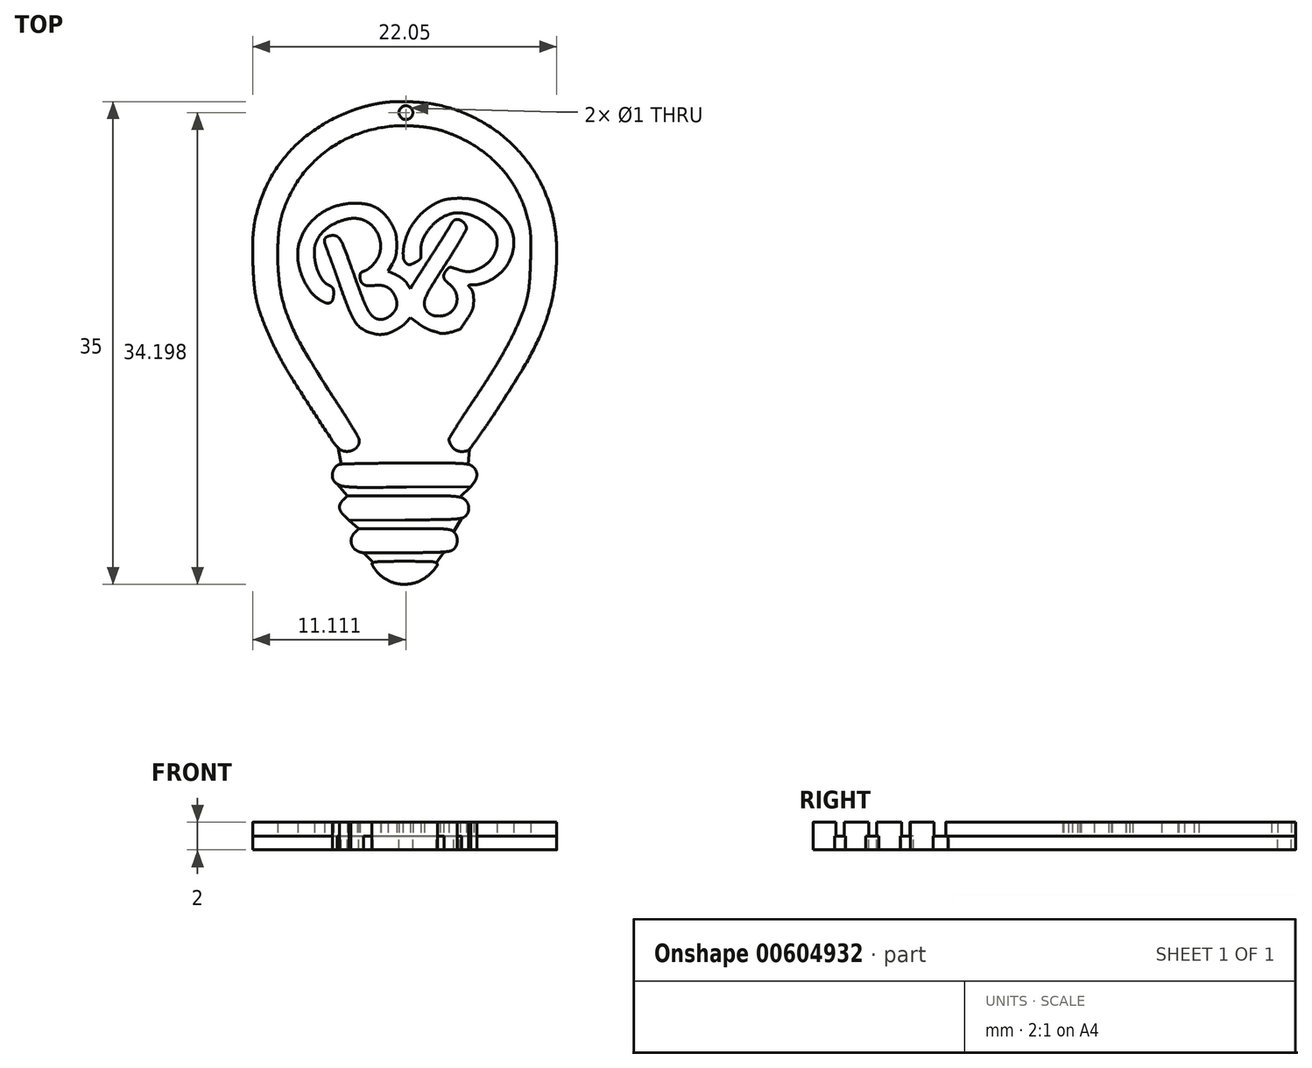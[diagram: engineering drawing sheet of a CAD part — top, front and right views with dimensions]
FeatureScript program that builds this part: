
annotation { "Feature Type Name" : "Feature", "Feature Type Description" : "" }
export const myFeature = defineFeature(function(context is Context, id is Id, definition is map)
    precondition{}
    {
        {
            var Q0;
            Q0=qCreatedBy(makeId("Top.planeOp"),FACE);
            var sketch = newSketch(context, id + "F0", { "sketchPlane" : qUnion([Q0])});
            skArc(sketch, "E0", {"start": v(-18.77, 20.13) * mm, "mid": v(-19.22, 20.06) * mm, "end": v(-19.67, 19.97) * mm});
            skArc(sketch, "E1", {"start": v(-19.67, 19.97) * mm, "mid": v(-20.1, 19.88) * mm, "end": v(-20.5, 19.76) * mm});
            skArc(sketch, "E2", {"start": v(-20.5, 19.76) * mm, "mid": v(-20.92, 19.63) * mm, "end": v(-21.33, 19.48) * mm});
            skArc(sketch, "E3", {"start": v(-21.33, 19.48) * mm, "mid": v(-21.77, 19.3) * mm, "end": v(-22.2, 19.1) * mm});
            skArc(sketch, "E4", {"start": v(-22.2, 19.1) * mm, "mid": v(-23.39, 18.47) * mm, "end": v(-24.49, 17.7) * mm});
            skArc(sketch, "E5", {"start": v(-24.49, 17.7) * mm, "mid": v(-25.46, 16.82) * mm, "end": v(-26.31, 15.83) * mm});
            skArc(sketch, "E6", {"start": v(-26.31, 15.83) * mm, "mid": v(-27.03, 14.75) * mm, "end": v(-27.6, 13.6) * mm});
            skArc(sketch, "E7", {"start": v(-27.6, 13.6) * mm, "mid": v(-28.02, 12.36) * mm, "end": v(-28.3, 11.08) * mm});
            skArc(sketch, "E8", {"start": v(-28.3, 11.08) * mm, "mid": v(-28.35, 10.53) * mm, "end": v(-28.38, 10) * mm});
            skArc(sketch, "E9", {"start": v(-28.38, 10) * mm, "mid": v(-28.38, 9.22) * mm, "end": v(-28.36, 8.44) * mm});
            skArc(sketch, "E10", {"start": v(-28.36, 8.44) * mm, "mid": v(-28.33, 7.67) * mm, "end": v(-28.27, 6.9) * mm});
            skArc(sketch, "E11", {"start": v(-28.27, 6.9) * mm, "mid": v(-28.21, 6.37) * mm, "end": v(-28.11, 5.84) * mm});
            skArc(sketch, "E12", {"start": v(-28.11, 5.84) * mm, "mid": v(-28, 5.38) * mm, "end": v(-27.86, 4.93) * mm});
            skArc(sketch, "E13", {"start": v(-27.86, 4.93) * mm, "mid": v(-27.67, 4.39) * mm, "end": v(-27.46, 3.85) * mm});
            skArc(sketch, "E14", {"start": v(-27.46, 3.85) * mm, "mid": v(-27.2, 3.27) * mm, "end": v(-26.94, 2.7) * mm});
            skArc(sketch, "E15", {"start": v(-26.94, 2.7) * mm, "mid": v(-26.66, 2.1) * mm, "end": v(-26.36, 1.53) * mm});
            skArc(sketch, "E16", {"start": v(-26.36, 1.53) * mm, "mid": v(-25.98, 0.88) * mm, "end": v(-25.6, 0.23) * mm});
            skArc(sketch, "E17", {"start": v(-25.6, 0.23) * mm, "mid": v(-24.89, -0.88) * mm, "end": v(-24.18, -2) * mm});
            skArc(sketch, "E18", {"start": v(-24.18, -2) * mm, "mid": v(-23.44, -3.12) * mm, "end": v(-22.7, -4.25) * mm});
            skArc(sketch, "E19", {"start": v(-22.7, -4.25) * mm, "mid": v(-22.46, -4.6) * mm, "end": v(-22.19, -4.91) * mm});
            skArc(sketch, "E20", {"start": v(-22.19, -4.91) * mm, "mid": v(-22, -5.07) * mm, "end": v(-21.76, -5.15) * mm});
            skArc(sketch, "E21", {"start": v(-21.76, -5.15) * mm, "mid": v(-21.5, -5.17) * mm, "end": v(-21.23, -5.13) * mm});
            skArc(sketch, "E22", {"start": v(-21.23, -5.13) * mm, "mid": v(-21, -5.02) * mm, "end": v(-20.8, -4.85) * mm});
            skArc(sketch, "E23", {"start": v(-20.8, -4.85) * mm, "mid": v(-20.69, -4.65) * mm, "end": v(-20.65, -4.43) * mm});
            skArc(sketch, "E24", {"start": v(-20.65, -4.43) * mm, "mid": v(-20.66, -4.3) * mm, "end": v(-20.7, -4.19) * mm});
            skArc(sketch, "E25", {"start": v(-20.7, -4.19) * mm, "mid": v(-20.88, -3.87) * mm, "end": v(-21.06, -3.55) * mm});
            skArc(sketch, "E26", {"start": v(-21.06, -3.55) * mm, "mid": v(-21.32, -3.13) * mm, "end": v(-21.58, -2.71) * mm});
            skArc(sketch, "E27", {"start": v(-21.58, -2.71) * mm, "mid": v(-21.94, -2.15) * mm, "end": v(-22.31, -1.58) * mm});
            skArc(sketch, "E28", {"start": v(-22.31, -1.58) * mm, "mid": v(-23.5, 0.26) * mm, "end": v(-24.63, 2.12) * mm});
            skArc(sketch, "E29", {"start": v(-24.63, 2.12) * mm, "mid": v(-25.3, 3.36) * mm, "end": v(-25.85, 4.64) * mm});
            skArc(sketch, "E30", {"start": v(-25.85, 4.64) * mm, "mid": v(-26.2, 5.76) * mm, "end": v(-26.42, 6.9) * mm});
            skArc(sketch, "E31", {"start": v(-26.42, 6.9) * mm, "mid": v(-26.54, 8.22) * mm, "end": v(-26.56, 9.55) * mm});
            skArc(sketch, "E32", {"start": v(-26.56, 9.55) * mm, "mid": v(-26.54, 10.12) * mm, "end": v(-26.5, 10.7) * mm});
            skArc(sketch, "E33", {"start": v(-26.5, 10.7) * mm, "mid": v(-26.44, 11.14) * mm, "end": v(-26.36, 11.58) * mm});
            skArc(sketch, "E34", {"start": v(-26.36, 11.58) * mm, "mid": v(-26.25, 12) * mm, "end": v(-26.11, 12.4) * mm});
            skArc(sketch, "E35", {"start": v(-26.11, 12.4) * mm, "mid": v(-25.93, 12.87) * mm, "end": v(-25.73, 13.33) * mm});
            skArc(sketch, "E36", {"start": v(-25.73, 13.33) * mm, "mid": v(-25.07, 14.49) * mm, "end": v(-24.24, 15.53) * mm});
            skArc(sketch, "E37", {"start": v(-24.24, 15.53) * mm, "mid": v(-23.26, 16.44) * mm, "end": v(-22.15, 17.2) * mm});
            skArc(sketch, "E38", {"start": v(-22.15, 17.2) * mm, "mid": v(-20.92, 17.78) * mm, "end": v(-19.62, 18.19) * mm});
            skArc(sketch, "E39", {"start": v(-19.62, 18.19) * mm, "mid": v(-18.26, 18.4) * mm, "end": v(-16.87, 18.43) * mm});
            skArc(sketch, "E40", {"start": v(-16.87, 18.43) * mm, "mid": v(-16.36, 18.39) * mm, "end": v(-15.84, 18.33) * mm});
            skArc(sketch, "E41", {"start": v(-15.84, 18.33) * mm, "mid": v(-15.4, 18.27) * mm, "end": v(-14.98, 18.17) * mm});
            skArc(sketch, "E42", {"start": v(-14.98, 18.17) * mm, "mid": v(-14.56, 18.05) * mm, "end": v(-14.16, 17.9) * mm});
            skArc(sketch, "E43", {"start": v(-14.16, 17.9) * mm, "mid": v(-13.7, 17.72) * mm, "end": v(-13.23, 17.51) * mm});
            skArc(sketch, "E44", {"start": v(-13.23, 17.51) * mm, "mid": v(-12.37, 17.04) * mm, "end": v(-11.55, 16.47) * mm});
            skArc(sketch, "E45", {"start": v(-11.55, 16.47) * mm, "mid": v(-10.82, 15.84) * mm, "end": v(-10.16, 15.12) * mm});
            skArc(sketch, "E46", {"start": v(-10.16, 15.12) * mm, "mid": v(-9.58, 14.34) * mm, "end": v(-9.1, 13.5) * mm});
            skArc(sketch, "E47", {"start": v(-9.1, 13.5) * mm, "mid": v(-8.71, 12.61) * mm, "end": v(-8.42, 11.68) * mm});
            skArc(sketch, "E48", {"start": v(-8.42, 11.68) * mm, "mid": v(-8.35, 11.38) * mm, "end": v(-8.3, 11.07) * mm});
            skArc(sketch, "E49", {"start": v(-8.3, 11.07) * mm, "mid": v(-8.25, 10.8) * mm, "end": v(-8.23, 10.52) * mm});
            skArc(sketch, "E50", {"start": v(-8.23, 10.52) * mm, "mid": v(-8.21, 10.17) * mm, "end": v(-8.2, 9.82) * mm});
            skArc(sketch, "E51", {"start": v(-8.2, 9.82) * mm, "mid": v(-8.22, 9.22) * mm, "end": v(-8.23, 8.62) * mm});
            skArc(sketch, "E52", {"start": v(-8.23, 8.62) * mm, "mid": v(-8.26, 7.83) * mm, "end": v(-8.31, 7.03) * mm});
            skArc(sketch, "E53", {"start": v(-8.31, 7.03) * mm, "mid": v(-8.37, 6.49) * mm, "end": v(-8.47, 5.95) * mm});
            skArc(sketch, "E54", {"start": v(-8.47, 5.95) * mm, "mid": v(-8.6, 5.44) * mm, "end": v(-8.78, 4.95) * mm});
            skArc(sketch, "E55", {"start": v(-8.78, 4.95) * mm, "mid": v(-9.04, 4.3) * mm, "end": v(-9.32, 3.68) * mm});
            skArc(sketch, "E56", {"start": v(-9.32, 3.68) * mm, "mid": v(-9.6, 3.08) * mm, "end": v(-9.91, 2.5) * mm});
            skArc(sketch, "E57", {"start": v(-9.91, 2.5) * mm, "mid": v(-10.26, 1.87) * mm, "end": v(-10.62, 1.25) * mm});
            skArc(sketch, "E58", {"start": v(-10.62, 1.25) * mm, "mid": v(-11.06, 0.53) * mm, "end": v(-11.51, -0.18) * mm});
            skArc(sketch, "E59", {"start": v(-11.51, -0.18) * mm, "mid": v(-12.09, -1.06) * mm, "end": v(-12.68, -1.94) * mm});
            skArc(sketch, "E60", {"start": v(-12.68, -1.94) * mm, "mid": v(-12.96, -2.36) * mm, "end": v(-13.24, -2.79) * mm});
            skArc(sketch, "E61", {"start": v(-13.24, -2.79) * mm, "mid": v(-13.48, -3.16) * mm, "end": v(-13.71, -3.54) * mm});
            skArc(sketch, "E62", {"start": v(-13.71, -3.54) * mm, "mid": v(-13.9, -3.86) * mm, "end": v(-14.1, -4.18) * mm});
            skArc(sketch, "E63", {"start": v(-14.1, -4.18) * mm, "mid": v(-14.13, -4.25) * mm, "end": v(-14.14, -4.33) * mm});
            skArc(sketch, "E64", {"start": v(-14.14, -4.33) * mm, "mid": v(-14.14, -4.38) * mm, "end": v(-14.12, -4.44) * mm});
            skArc(sketch, "E65", {"start": v(-14.12, -4.44) * mm, "mid": v(-14.1, -4.5) * mm, "end": v(-14.07, -4.58) * mm});
            skArc(sketch, "E66", {"start": v(-14.07, -4.58) * mm, "mid": v(-14.03, -4.66) * mm, "end": v(-13.99, -4.73) * mm});
            skArc(sketch, "E67", {"start": v(-13.99, -4.73) * mm, "mid": v(-13.94, -4.8) * mm, "end": v(-13.9, -4.87) * mm});
            skArc(sketch, "E68", {"start": v(-13.9, -4.87) * mm, "mid": v(-13.8, -4.97) * mm, "end": v(-13.68, -5.06) * mm});
            skArc(sketch, "E69", {"start": v(-13.68, -5.06) * mm, "mid": v(-13.55, -5.12) * mm, "end": v(-13.4, -5.16) * mm});
            skArc(sketch, "E70", {"start": v(-13.4, -5.16) * mm, "mid": v(-13.25, -5.18) * mm, "end": v(-13.1, -5.18) * mm});
            skArc(sketch, "E71", {"start": v(-13.1, -5.18) * mm, "mid": v(-12.93, -5.15) * mm, "end": v(-12.77, -5.1) * mm});
            skArc(sketch, "E72", {"start": v(-12.77, -5.1) * mm, "mid": v(-12.7, -5.07) * mm, "end": v(-12.66, -5.01) * mm});
            skArc(sketch, "E73", {"start": v(-12.66, -5.01) * mm, "mid": v(-12.42, -4.7) * mm, "end": v(-12.2, -4.38) * mm});
            skArc(sketch, "E74", {"start": v(-12.2, -4.38) * mm, "mid": v(-11.92, -4) * mm, "end": v(-11.66, -3.63) * mm});
            skArc(sketch, "E75", {"start": v(-11.66, -3.63) * mm, "mid": v(-11.36, -3.2) * mm, "end": v(-11.06, -2.76) * mm});
            skArc(sketch, "E76", {"start": v(-11.06, -2.76) * mm, "mid": v(-9.94, -1.04) * mm, "end": v(-8.86, 0.7) * mm});
            skArc(sketch, "E77", {"start": v(-8.86, 0.7) * mm, "mid": v(-8.17, 1.92) * mm, "end": v(-7.55, 3.19) * mm});
            skArc(sketch, "E78", {"start": v(-7.55, 3.19) * mm, "mid": v(-7.13, 4.24) * mm, "end": v(-6.8, 5.33) * mm});
            skArc(sketch, "E79", {"start": v(-6.8, 5.33) * mm, "mid": v(-6.55, 6.45) * mm, "end": v(-6.4, 7.58) * mm});
            skArc(sketch, "E80", {"start": v(-6.4, 7.58) * mm, "mid": v(-6.35, 8.52) * mm, "end": v(-6.33, 9.46) * mm});
            skArc(sketch, "E81", {"start": v(-6.33, 9.46) * mm, "mid": v(-6.37, 10.3) * mm, "end": v(-6.47, 11.12) * mm});
            skArc(sketch, "E82", {"start": v(-6.47, 11.12) * mm, "mid": v(-6.62, 11.9) * mm, "end": v(-6.82, 12.65) * mm});
            skArc(sketch, "E83", {"start": v(-6.82, 12.65) * mm, "mid": v(-7.1, 13.4) * mm, "end": v(-7.4, 14.13) * mm});
            skArc(sketch, "E84", {"start": v(-7.4, 14.13) * mm, "mid": v(-8, 15.19) * mm, "end": v(-8.71, 16.17) * mm});
            skArc(sketch, "E85", {"start": v(-8.71, 16.17) * mm, "mid": v(-9.55, 17.07) * mm, "end": v(-10.48, 17.88) * mm});
            skArc(sketch, "E86", {"start": v(-10.48, 17.88) * mm, "mid": v(-11.51, 18.59) * mm, "end": v(-12.61, 19.17) * mm});
            skArc(sketch, "E87", {"start": v(-12.61, 19.17) * mm, "mid": v(-13.77, 19.63) * mm, "end": v(-14.97, 19.95) * mm});
            skArc(sketch, "E88", {"start": v(-14.97, 19.95) * mm, "mid": v(-15.41, 20.03) * mm, "end": v(-15.86, 20.1) * mm});
            skArc(sketch, "E89", {"start": v(-15.86, 20.1) * mm, "mid": v(-16.39, 20.14) * mm, "end": v(-16.91, 20.17) * mm});
            skArc(sketch, "E90", {"start": v(-16.91, 20.17) * mm, "mid": v(-17.43, 20.2) * mm, "end": v(-17.95, 20.2) * mm});
            skArc(sketch, "E91", {"start": v(-17.95, 20.2) * mm, "mid": v(-18.36, 20.17) * mm, "end": v(-18.77, 20.13) * mm});
            skArc(sketch, "E92", {"start": v(-22.18, -6.15) * mm, "mid": v(-22.3, -6.22) * mm, "end": v(-22.4, -6.32) * mm});
            skArc(sketch, "E93", {"start": v(-22.4, -6.32) * mm, "mid": v(-22.48, -6.45) * mm, "end": v(-22.54, -6.58) * mm});
            skArc(sketch, "E94", {"start": v(-22.54, -6.58) * mm, "mid": v(-22.59, -6.73) * mm, "end": v(-22.6, -6.89) * mm});
            skArc(sketch, "E95", {"start": v(-22.6, -6.89) * mm, "mid": v(-22.6, -7.03) * mm, "end": v(-22.57, -7.16) * mm});
            skArc(sketch, "E96", {"start": v(-22.57, -7.16) * mm, "mid": v(-22.44, -7.37) * mm, "end": v(-22.26, -7.53) * mm});
            skArc(sketch, "E97", {"start": v(-22.26, -7.53) * mm, "mid": v(-21.99, -7.65) * mm, "end": v(-21.7, -7.72) * mm});
            skArc(sketch, "E98", {"start": v(-21.7, -7.72) * mm, "mid": v(-21.14, -7.76) * mm, "end": v(-20.58, -7.78) * mm});
            skArc(sketch, "E99", {"start": v(-20.58, -7.78) * mm, "mid": v(-18.9, -7.78) * mm, "end": v(-17.23, -7.77) * mm});
            skLineSegment(sketch, "E100", {"start": v(-17.23, -7.77) * mm, "end": v(-12.58, -7.73) * mm});
            skLineSegment(sketch, "E101", {"start": v(-12.58, -7.73) * mm, "end": v(-12.35, -7.45) * mm});
            skArc(sketch, "E102", {"start": v(-12.35, -7.45) * mm, "mid": v(-12.25, -7.3) * mm, "end": v(-12.17, -7.14) * mm});
            skArc(sketch, "E103", {"start": v(-12.17, -7.14) * mm, "mid": v(-12.13, -6.98) * mm, "end": v(-12.13, -6.81) * mm});
            skArc(sketch, "E104", {"start": v(-12.13, -6.81) * mm, "mid": v(-12.16, -6.66) * mm, "end": v(-12.22, -6.5) * mm});
            skArc(sketch, "E105", {"start": v(-12.22, -6.5) * mm, "mid": v(-12.31, -6.37) * mm, "end": v(-12.43, -6.26) * mm});
            skArc(sketch, "E106", {"start": v(-12.43, -6.26) * mm, "mid": v(-12.59, -6.16) * mm, "end": v(-12.76, -6.1) * mm});
            skArc(sketch, "E107", {"start": v(-12.76, -6.1) * mm, "mid": v(-13.04, -6.07) * mm, "end": v(-13.32, -6.04) * mm});
            skArc(sketch, "E108", {"start": v(-13.32, -6.04) * mm, "mid": v(-13.85, -6.03) * mm, "end": v(-14.38, -6.02) * mm});
            skArc(sketch, "E109", {"start": v(-14.38, -6.02) * mm, "mid": v(-15.86, -6.02) * mm, "end": v(-17.34, -6.02) * mm});
            skArc(sketch, "E110", {"start": v(-17.34, -6.02) * mm, "mid": v(-18.34, -6.02) * mm, "end": v(-19.34, -6.03) * mm});
            skArc(sketch, "E111", {"start": v(-19.34, -6.03) * mm, "mid": v(-20.07, -6.04) * mm, "end": v(-20.81, -6.06) * mm});
            skArc(sketch, "E112", {"start": v(-20.81, -6.06) * mm, "mid": v(-21.38, -6.07) * mm, "end": v(-21.95, -6.1) * mm});
            skArc(sketch, "E113", {"start": v(-21.95, -6.1) * mm, "mid": v(-22.07, -6.11) * mm, "end": v(-22.18, -6.15) * mm});
            skArc(sketch, "E114", {"start": v(-21.81, -8.68) * mm, "mid": v(-21.93, -8.81) * mm, "end": v(-22.02, -8.96) * mm});
            skArc(sketch, "E115", {"start": v(-22.02, -8.96) * mm, "mid": v(-22.07, -9.1) * mm, "end": v(-22.09, -9.24) * mm});
            skArc(sketch, "E116", {"start": v(-22.09, -9.24) * mm, "mid": v(-22.06, -9.38) * mm, "end": v(-22, -9.52) * mm});
            skArc(sketch, "E117", {"start": v(-22, -9.52) * mm, "mid": v(-21.88, -9.68) * mm, "end": v(-21.75, -9.83) * mm});
            skLineSegment(sketch, "E118", {"start": v(-21.75, -9.83) * mm, "end": v(-21.4, -10.18) * mm});
            skLineSegment(sketch, "E119", {"start": v(-21.4, -10.18) * mm, "end": v(-17.3, -10.14) * mm});
            skArc(sketch, "E120", {"start": v(-17.3, -10.14) * mm, "mid": v(-16.05, -10.13) * mm, "end": v(-14.8, -10.12) * mm});
            skArc(sketch, "E121", {"start": v(-14.8, -10.12) * mm, "mid": v(-14.29, -10.1) * mm, "end": v(-13.79, -10.08) * mm});
            skArc(sketch, "E122", {"start": v(-13.79, -10.08) * mm, "mid": v(-13.51, -10.06) * mm, "end": v(-13.24, -10.02) * mm});
            skArc(sketch, "E123", {"start": v(-13.24, -10.02) * mm, "mid": v(-13.1, -9.97) * mm, "end": v(-12.97, -9.88) * mm});
            skArc(sketch, "E124", {"start": v(-12.97, -9.88) * mm, "mid": v(-12.85, -9.75) * mm, "end": v(-12.77, -9.6) * mm});
            skArc(sketch, "E125", {"start": v(-12.77, -9.6) * mm, "mid": v(-12.72, -9.43) * mm, "end": v(-12.71, -9.25) * mm});
            skArc(sketch, "E126", {"start": v(-12.71, -9.25) * mm, "mid": v(-12.74, -9.07) * mm, "end": v(-12.8, -8.9) * mm});
            skArc(sketch, "E127", {"start": v(-12.8, -8.9) * mm, "mid": v(-12.9, -8.76) * mm, "end": v(-13.03, -8.63) * mm});
            skArc(sketch, "E128", {"start": v(-13.03, -8.63) * mm, "mid": v(-13.18, -8.54) * mm, "end": v(-13.34, -8.49) * mm});
            skArc(sketch, "E129", {"start": v(-13.34, -8.49) * mm, "mid": v(-13.6, -8.44) * mm, "end": v(-13.86, -8.42) * mm});
            skArc(sketch, "E130", {"start": v(-13.86, -8.42) * mm, "mid": v(-14.34, -8.4) * mm, "end": v(-14.82, -8.4) * mm});
            skArc(sketch, "E131", {"start": v(-14.82, -8.4) * mm, "mid": v(-16.12, -8.39) * mm, "end": v(-17.43, -8.39) * mm});
            skLineSegment(sketch, "E132", {"start": v(-17.43, -8.39) * mm, "end": v(-21.52, -8.39) * mm});
            skLineSegment(sketch, "E133", {"start": v(-21.52, -8.39) * mm, "end": v(-21.81, -8.68) * mm});
            skArc(sketch, "E134", {"start": v(-20.98, -11.05) * mm, "mid": v(-21.12, -11.24) * mm, "end": v(-21.22, -11.45) * mm});
            skArc(sketch, "E135", {"start": v(-21.22, -11.45) * mm, "mid": v(-21.25, -11.67) * mm, "end": v(-21.21, -11.9) * mm});
            skArc(sketch, "E136", {"start": v(-21.21, -11.9) * mm, "mid": v(-21.11, -12.1) * mm, "end": v(-20.96, -12.27) * mm});
            skArc(sketch, "E137", {"start": v(-20.96, -12.27) * mm, "mid": v(-20.76, -12.4) * mm, "end": v(-20.53, -12.49) * mm});
            skArc(sketch, "E138", {"start": v(-20.53, -12.49) * mm, "mid": v(-20.43, -12.5) * mm, "end": v(-20.33, -12.51) * mm});
            skArc(sketch, "E139", {"start": v(-20.33, -12.51) * mm, "mid": v(-19.88, -12.52) * mm, "end": v(-19.42, -12.53) * mm});
            skArc(sketch, "E140", {"start": v(-19.42, -12.53) * mm, "mid": v(-18.9, -12.53) * mm, "end": v(-18.36, -12.53) * mm});
            skArc(sketch, "E141", {"start": v(-18.36, -12.53) * mm, "mid": v(-17.76, -12.53) * mm, "end": v(-17.15, -12.52) * mm});
            skArc(sketch, "E142", {"start": v(-17.15, -12.52) * mm, "mid": v(-16.22, -12.5) * mm, "end": v(-15.28, -12.5) * mm});
            skArc(sketch, "E143", {"start": v(-15.28, -12.5) * mm, "mid": v(-14.88, -12.48) * mm, "end": v(-14.49, -12.46) * mm});
            skArc(sketch, "E144", {"start": v(-14.49, -12.46) * mm, "mid": v(-14.27, -12.43) * mm, "end": v(-14.05, -12.39) * mm});
            skArc(sketch, "E145", {"start": v(-14.05, -12.39) * mm, "mid": v(-13.91, -12.34) * mm, "end": v(-13.8, -12.26) * mm});
            skArc(sketch, "E146", {"start": v(-13.8, -12.26) * mm, "mid": v(-13.69, -12.14) * mm, "end": v(-13.61, -12) * mm});
            skArc(sketch, "E147", {"start": v(-13.61, -12) * mm, "mid": v(-13.57, -11.82) * mm, "end": v(-13.55, -11.64) * mm});
            skArc(sketch, "E148", {"start": v(-13.55, -11.64) * mm, "mid": v(-13.56, -11.46) * mm, "end": v(-13.6, -11.28) * mm});
            skArc(sketch, "E149", {"start": v(-13.6, -11.28) * mm, "mid": v(-13.68, -11.13) * mm, "end": v(-13.78, -11) * mm});
            skArc(sketch, "E150", {"start": v(-13.78, -11) * mm, "mid": v(-13.9, -10.91) * mm, "end": v(-14.03, -10.86) * mm});
            skArc(sketch, "E151", {"start": v(-14.03, -10.86) * mm, "mid": v(-14.25, -10.82) * mm, "end": v(-14.46, -10.8) * mm});
            skArc(sketch, "E152", {"start": v(-14.46, -10.8) * mm, "mid": v(-14.86, -10.78) * mm, "end": v(-15.27, -10.77) * mm});
            skArc(sketch, "E153", {"start": v(-15.27, -10.77) * mm, "mid": v(-16.3, -10.76) * mm, "end": v(-17.35, -10.76) * mm});
            skLineSegment(sketch, "E154", {"start": v(-17.35, -10.76) * mm, "end": v(-20.69, -10.76) * mm});
            skLineSegment(sketch, "E155", {"start": v(-20.69, -10.76) * mm, "end": v(-20.98, -11.05) * mm});
            skArc(sketch, "E156", {"start": v(-19.73, -13.31) * mm, "mid": v(-19.72, -13.36) * mm, "end": v(-19.7, -13.4) * mm});
            skArc(sketch, "E157", {"start": v(-19.7, -13.4) * mm, "mid": v(-19.66, -13.49) * mm, "end": v(-19.61, -13.57) * mm});
            skArc(sketch, "E158", {"start": v(-19.61, -13.57) * mm, "mid": v(-19.55, -13.66) * mm, "end": v(-19.49, -13.75) * mm});
            skArc(sketch, "E159", {"start": v(-19.49, -13.75) * mm, "mid": v(-19.42, -13.84) * mm, "end": v(-19.34, -13.93) * mm});
            skArc(sketch, "E160", {"start": v(-19.34, -13.93) * mm, "mid": v(-18.95, -14.3) * mm, "end": v(-18.49, -14.56) * mm});
            skArc(sketch, "E161", {"start": v(-18.49, -14.56) * mm, "mid": v(-17.98, -14.74) * mm, "end": v(-17.45, -14.8) * mm});
            skArc(sketch, "E162", {"start": v(-17.45, -14.8) * mm, "mid": v(-16.9, -14.76) * mm, "end": v(-16.39, -14.6) * mm});
            skArc(sketch, "E163", {"start": v(-16.39, -14.6) * mm, "mid": v(-15.9, -14.35) * mm, "end": v(-15.48, -14) * mm});
            skArc(sketch, "E164", {"start": v(-15.48, -14) * mm, "mid": v(-15.24, -13.75) * mm, "end": v(-15.02, -13.47) * mm});
            skArc(sketch, "E165", {"start": v(-15.02, -13.47) * mm, "mid": v(-15, -13.35) * mm, "end": v(-15.07, -13.25) * mm});
            skArc(sketch, "E166", {"start": v(-15.07, -13.25) * mm, "mid": v(-15.29, -13.18) * mm, "end": v(-15.51, -13.15) * mm});
            skArc(sketch, "E167", {"start": v(-15.51, -13.15) * mm, "mid": v(-16.43, -13.14) * mm, "end": v(-17.35, -13.14) * mm});
            skArc(sketch, "E168", {"start": v(-17.35, -13.14) * mm, "mid": v(-18, -13.14) * mm, "end": v(-18.66, -13.15) * mm});
            skArc(sketch, "E169", {"start": v(-18.66, -13.15) * mm, "mid": v(-18.97, -13.15) * mm, "end": v(-19.3, -13.17) * mm});
            skArc(sketch, "E170", {"start": v(-19.3, -13.17) * mm, "mid": v(-19.47, -13.19) * mm, "end": v(-19.65, -13.22) * mm});
            skArc(sketch, "E171", {"start": v(-19.65, -13.22) * mm, "mid": v(-19.7, -13.25) * mm, "end": v(-19.73, -13.31) * mm});
            skLineSegment(sketch, "E172", {"start": v(-22.19, -4.91) * mm, "end": v(-21.95, -6.1) * mm});
            skLineSegment(sketch, "E173", {"start": v(-12.66, -5.01) * mm, "end": v(-12.76, -6.1) * mm});
            skLineSegment(sketch, "E174", {"start": v(-22.26, -7.53) * mm, "end": v(-21.52, -8.39) * mm});
            skLineSegment(sketch, "E175", {"start": v(-12.58, -7.73) * mm, "end": v(-13.34, -8.49) * mm});
            skLineSegment(sketch, "E176", {"start": v(-13.24, -10.02) * mm, "end": v(-13.78, -11) * mm});
            skLineSegment(sketch, "E177", {"start": v(-21.4, -10.18) * mm, "end": v(-20.69, -10.76) * mm});
            skLineSegment(sketch, "E178", {"start": v(-20.33, -12.51) * mm, "end": v(-19.65, -13.22) * mm});
            skLineSegment(sketch, "E179", {"start": v(-14.49, -12.46) * mm, "end": v(-15.07, -13.25) * mm});
            skSolve(sketch);
        }
        {
            var Q0;
            Q0 = qSketchRegion(id + "F0", true);
            extrude(context, id + "F1", {"entities" : qUnion([Q0]), "oppositeDirection" : true, "depth" : 1 * mm, "offsetDistance" : 25.4 * mm});
        }
        {
            var Q0;
            Q0=makeQuery(id+"F0.imprint","IMPRINT",FACE,{"disambiguationData":[TD([[makeQuery(id+"F0.imprint","IMPRINT",EDGE,{"derivedFrom":sQuery(id+"F0.wireOp",EDGE,"E0")}),1.0]])]});
            extrude(context, id + "F2", {"entities" : qUnion([Q0]), "depth" : 1 * mm, "offsetDistance" : 25.4 * mm});
        }
        {
            var Q0;
            Q0=makeQuery(id+"F0.imprint","IMPRINT",FACE,{"disambiguationData":[TD([[makeQuery(id+"F0.imprint","IMPRINT",EDGE,{"derivedFrom":sQuery(id+"F0.wireOp",EDGE,"E92")}),1.0]])]});
            var Q1;
            Q1=makeQuery(id+"F0.imprint","IMPRINT",FACE,{"disambiguationData":[TD([[makeQuery(id+"F0.imprint","IMPRINT",EDGE,{"derivedFrom":sQuery(id+"F0.wireOp",EDGE,"E114")}),1.0]])]});
            var Q2;
            Q2=makeQuery(id+"F0.imprint","IMPRINT",FACE,{"disambiguationData":[TD([[makeQuery(id+"F0.imprint","IMPRINT",EDGE,{"derivedFrom":sQuery(id+"F0.wireOp",EDGE,"E134")}),1.0]])]});
            var Q3;
            Q3=makeQuery(id+"F0.imprint","IMPRINT",FACE,{"disambiguationData":[TD([[makeQuery(id+"F0.imprint","IMPRINT",EDGE,{"derivedFrom":sQuery(id+"F0.wireOp",EDGE,"E156")}),1.0]])]});
            extrude(context, id + "F3", {"entities" : qUnion([Q0, Q1, Q2, Q3]), "operationType" : NewBodyOperationType.ADD, "depth" : 1 * mm, "offsetDistance" : 25.4 * mm});
        }
        {
            var Q0;
            Q0=qCreatedBy(makeId("Top.planeOp"),FACE);
            var sketch = newSketch(context, id + "F4", { "sketchPlane" : qUnion([Q0])});
            skArc(sketch, "E180", {"start": v(-14.75, 12.98) * mm, "mid": v(-15.04, 12.85) * mm, "end": v(-15.32, 12.7) * mm});
            skArc(sketch, "E181", {"start": v(-15.32, 12.7) * mm, "mid": v(-15.59, 12.53) * mm, "end": v(-15.84, 12.34) * mm});
            skArc(sketch, "E182", {"start": v(-15.84, 12.34) * mm, "mid": v(-16.09, 12.13) * mm, "end": v(-16.31, 11.9) * mm});
            skArc(sketch, "E183", {"start": v(-16.31, 11.9) * mm, "mid": v(-16.53, 11.65) * mm, "end": v(-16.72, 11.4) * mm});
            skArc(sketch, "E184", {"start": v(-16.72, 11.4) * mm, "mid": v(-16.97, 10.99) * mm, "end": v(-17.17, 10.56) * mm});
            skArc(sketch, "E185", {"start": v(-17.17, 10.56) * mm, "mid": v(-17.32, 10.12) * mm, "end": v(-17.43, 9.67) * mm});
            skArc(sketch, "E186", {"start": v(-17.43, 9.67) * mm, "mid": v(-17.47, 9.28) * mm, "end": v(-17.46, 8.9) * mm});
            skArc(sketch, "E187", {"start": v(-17.46, 8.9) * mm, "mid": v(-17.38, 8.64) * mm, "end": v(-17.22, 8.44) * mm});
            skArc(sketch, "E188", {"start": v(-17.22, 8.44) * mm, "mid": v(-17.16, 8.4) * mm, "end": v(-17.1, 8.38) * mm});
            skArc(sketch, "E189", {"start": v(-17.1, 8.38) * mm, "mid": v(-17.05, 8.37) * mm, "end": v(-16.99, 8.37) * mm});
            skArc(sketch, "E190", {"start": v(-16.99, 8.37) * mm, "mid": v(-16.9, 8.39) * mm, "end": v(-16.83, 8.42) * mm});
            skArc(sketch, "E191", {"start": v(-16.83, 8.42) * mm, "mid": v(-16.71, 8.47) * mm, "end": v(-16.6, 8.53) * mm});
            skArc(sketch, "E192", {"start": v(-16.6, 8.53) * mm, "mid": v(-16.46, 8.6) * mm, "end": v(-16.33, 8.68) * mm});
            skArc(sketch, "E193", {"start": v(-16.33, 8.68) * mm, "mid": v(-16.27, 8.74) * mm, "end": v(-16.22, 8.8) * mm});
            skArc(sketch, "E194", {"start": v(-16.22, 8.8) * mm, "mid": v(-16.19, 8.88) * mm, "end": v(-16.18, 8.96) * mm});
            skArc(sketch, "E195", {"start": v(-16.18, 8.96) * mm, "mid": v(-16.18, 9.1) * mm, "end": v(-16.18, 9.25) * mm});
            skArc(sketch, "E196", {"start": v(-16.18, 9.25) * mm, "mid": v(-16.16, 9.75) * mm, "end": v(-16.01, 10.24) * mm});
            skArc(sketch, "E197", {"start": v(-16.01, 10.24) * mm, "mid": v(-15.74, 10.74) * mm, "end": v(-15.38, 11.19) * mm});
            skArc(sketch, "E198", {"start": v(-15.38, 11.19) * mm, "mid": v(-14.95, 11.57) * mm, "end": v(-14.46, 11.88) * mm});
            skArc(sketch, "E199", {"start": v(-14.46, 11.88) * mm, "mid": v(-13.99, 12.06) * mm, "end": v(-13.48, 12.12) * mm});
            skArc(sketch, "E200", {"start": v(-13.48, 12.12) * mm, "mid": v(-13.03, 12.09) * mm, "end": v(-12.6, 11.98) * mm});
            skArc(sketch, "E201", {"start": v(-12.6, 11.98) * mm, "mid": v(-12.13, 11.78) * mm, "end": v(-11.7, 11.54) * mm});
            skArc(sketch, "E202", {"start": v(-11.7, 11.54) * mm, "mid": v(-11.33, 11.26) * mm, "end": v(-11, 10.93) * mm});
            skArc(sketch, "E203", {"start": v(-11, 10.93) * mm, "mid": v(-10.8, 10.64) * mm, "end": v(-10.68, 10.3) * mm});
            skArc(sketch, "E204", {"start": v(-10.68, 10.3) * mm, "mid": v(-10.65, 9.97) * mm, "end": v(-10.68, 9.64) * mm});
            skArc(sketch, "E205", {"start": v(-10.68, 9.64) * mm, "mid": v(-10.77, 9.32) * mm, "end": v(-10.92, 9) * mm});
            skArc(sketch, "E206", {"start": v(-10.92, 9) * mm, "mid": v(-11.12, 8.72) * mm, "end": v(-11.37, 8.47) * mm});
            skArc(sketch, "E207", {"start": v(-11.37, 8.47) * mm, "mid": v(-11.66, 8.24) * mm, "end": v(-11.99, 8.07) * mm});
            skArc(sketch, "E208", {"start": v(-11.99, 8.07) * mm, "mid": v(-12.19, 7.98) * mm, "end": v(-12.4, 7.91) * mm});
            skArc(sketch, "E209", {"start": v(-12.4, 7.91) * mm, "mid": v(-12.56, 7.88) * mm, "end": v(-12.72, 7.86) * mm});
            skArc(sketch, "E210", {"start": v(-12.72, 7.86) * mm, "mid": v(-12.9, 7.87) * mm, "end": v(-13.07, 7.9) * mm});
            skArc(sketch, "E211", {"start": v(-13.07, 7.9) * mm, "mid": v(-13.31, 7.96) * mm, "end": v(-13.55, 8.04) * mm});
            skArc(sketch, "E212", {"start": v(-13.55, 8.04) * mm, "mid": v(-13.73, 8.1) * mm, "end": v(-13.91, 8.15) * mm});
            skArc(sketch, "E213", {"start": v(-13.91, 8.15) * mm, "mid": v(-14, 8.17) * mm, "end": v(-14.07, 8.17) * mm});
            skArc(sketch, "E214", {"start": v(-14.07, 8.17) * mm, "mid": v(-14.13, 8.15) * mm, "end": v(-14.18, 8.12) * mm});
            skArc(sketch, "E215", {"start": v(-14.18, 8.12) * mm, "mid": v(-14.26, 8.04) * mm, "end": v(-14.33, 7.97) * mm});
            skArc(sketch, "E216", {"start": v(-14.33, 7.97) * mm, "mid": v(-14.42, 7.83) * mm, "end": v(-14.5, 7.7) * mm});
            skArc(sketch, "E217", {"start": v(-14.5, 7.7) * mm, "mid": v(-14.53, 7.57) * mm, "end": v(-14.52, 7.45) * mm});
            skArc(sketch, "E218", {"start": v(-14.52, 7.45) * mm, "mid": v(-14.48, 7.33) * mm, "end": v(-14.4, 7.22) * mm});
            skArc(sketch, "E219", {"start": v(-14.4, 7.22) * mm, "mid": v(-14.27, 7.09) * mm, "end": v(-14.13, 6.97) * mm});
            skArc(sketch, "E220", {"start": v(-14.13, 6.97) * mm, "mid": v(-13.83, 6.67) * mm, "end": v(-13.63, 6.3) * mm});
            skArc(sketch, "E221", {"start": v(-13.63, 6.3) * mm, "mid": v(-13.56, 5.9) * mm, "end": v(-13.61, 5.5) * mm});
            skArc(sketch, "E222", {"start": v(-13.61, 5.5) * mm, "mid": v(-13.8, 5.15) * mm, "end": v(-14.08, 4.88) * mm});
            skArc(sketch, "E223", {"start": v(-14.08, 4.88) * mm, "mid": v(-14.45, 4.7) * mm, "end": v(-14.85, 4.64) * mm});
            skArc(sketch, "E224", {"start": v(-14.85, 4.64) * mm, "mid": v(-14.99, 4.64) * mm, "end": v(-15.13, 4.65) * mm});
            skArc(sketch, "E225", {"start": v(-15.13, 4.65) * mm, "mid": v(-15.23, 4.67) * mm, "end": v(-15.33, 4.7) * mm});
            skArc(sketch, "E226", {"start": v(-15.33, 4.7) * mm, "mid": v(-15.42, 4.74) * mm, "end": v(-15.5, 4.79) * mm});
            skArc(sketch, "E227", {"start": v(-15.5, 4.79) * mm, "mid": v(-15.6, 4.86) * mm, "end": v(-15.68, 4.93) * mm});
            skArc(sketch, "E228", {"start": v(-15.68, 4.93) * mm, "mid": v(-15.83, 5.14) * mm, "end": v(-15.92, 5.38) * mm});
            skArc(sketch, "E229", {"start": v(-15.92, 5.38) * mm, "mid": v(-15.93, 5.64) * mm, "end": v(-15.87, 5.9) * mm});
            skArc(sketch, "E230", {"start": v(-15.87, 5.9) * mm, "mid": v(-15.69, 6.32) * mm, "end": v(-15.46, 6.72) * mm});
            skArc(sketch, "E231", {"start": v(-15.46, 6.72) * mm, "mid": v(-14.87, 7.67) * mm, "end": v(-14.26, 8.62) * mm});
            skArc(sketch, "E232", {"start": v(-14.26, 8.62) * mm, "mid": v(-14, 9.04) * mm, "end": v(-13.73, 9.46) * mm});
            skArc(sketch, "E233", {"start": v(-13.73, 9.46) * mm, "mid": v(-13.5, 9.83) * mm, "end": v(-13.29, 10.2) * mm});
            skArc(sketch, "E234", {"start": v(-13.29, 10.2) * mm, "mid": v(-13.1, 10.52) * mm, "end": v(-12.92, 10.84) * mm});
            skArc(sketch, "E235", {"start": v(-12.92, 10.84) * mm, "mid": v(-12.9, 10.92) * mm, "end": v(-12.88, 11) * mm});
            skArc(sketch, "E236", {"start": v(-12.88, 11) * mm, "mid": v(-12.9, 11.12) * mm, "end": v(-12.94, 11.23) * mm});
            skArc(sketch, "E237", {"start": v(-12.94, 11.23) * mm, "mid": v(-13, 11.35) * mm, "end": v(-13.1, 11.44) * mm});
            skArc(sketch, "E238", {"start": v(-13.1, 11.44) * mm, "mid": v(-13.2, 11.53) * mm, "end": v(-13.33, 11.6) * mm});
            skArc(sketch, "E239", {"start": v(-13.33, 11.6) * mm, "mid": v(-13.44, 11.64) * mm, "end": v(-13.57, 11.65) * mm});
            skArc(sketch, "E240", {"start": v(-13.57, 11.65) * mm, "mid": v(-13.63, 11.64) * mm, "end": v(-13.7, 11.62) * mm});
            skArc(sketch, "E241", {"start": v(-13.7, 11.62) * mm, "mid": v(-13.75, 11.6) * mm, "end": v(-13.8, 11.55) * mm});
            skArc(sketch, "E242", {"start": v(-13.8, 11.55) * mm, "mid": v(-13.87, 11.5) * mm, "end": v(-13.92, 11.43) * mm});
            skArc(sketch, "E243", {"start": v(-13.92, 11.43) * mm, "mid": v(-13.98, 11.35) * mm, "end": v(-14.02, 11.26) * mm});
            skArc(sketch, "E244", {"start": v(-14.02, 11.26) * mm, "mid": v(-14.09, 11.14) * mm, "end": v(-14.16, 11.02) * mm});
            skArc(sketch, "E245", {"start": v(-14.16, 11.02) * mm, "mid": v(-14.34, 10.74) * mm, "end": v(-14.51, 10.45) * mm});
            skArc(sketch, "E246", {"start": v(-14.51, 10.45) * mm, "mid": v(-14.73, 10.1) * mm, "end": v(-14.94, 9.77) * mm});
            skArc(sketch, "E247", {"start": v(-14.94, 9.77) * mm, "mid": v(-15.18, 9.4) * mm, "end": v(-15.41, 9.04) * mm});
            skArc(sketch, "E248", {"start": v(-15.41, 9.04) * mm, "mid": v(-15.65, 8.67) * mm, "end": v(-15.88, 8.3) * mm});
            skArc(sketch, "E249", {"start": v(-15.88, 8.3) * mm, "mid": v(-16.1, 7.98) * mm, "end": v(-16.3, 7.65) * mm});
            skArc(sketch, "E250", {"start": v(-16.3, 7.65) * mm, "mid": v(-16.48, 7.37) * mm, "end": v(-16.66, 7.1) * mm});
            skArc(sketch, "E251", {"start": v(-16.66, 7.1) * mm, "mid": v(-16.71, 7) * mm, "end": v(-16.77, 6.9) * mm});
            skLineSegment(sketch, "E252", {"start": v(-16.77, 6.9) * mm, "end": v(-16.95, 6.63) * mm});
            skLineSegment(sketch, "E253", {"start": v(-16.95, 6.63) * mm, "end": v(-17.18, 7) * mm});
            skArc(sketch, "E254", {"start": v(-17.18, 7) * mm, "mid": v(-17.24, 7.08) * mm, "end": v(-17.31, 7.16) * mm});
            skArc(sketch, "E255", {"start": v(-17.31, 7.16) * mm, "mid": v(-17.41, 7.25) * mm, "end": v(-17.51, 7.34) * mm});
            skArc(sketch, "E256", {"start": v(-17.51, 7.34) * mm, "mid": v(-17.63, 7.42) * mm, "end": v(-17.75, 7.5) * mm});
            skArc(sketch, "E257", {"start": v(-17.75, 7.5) * mm, "mid": v(-17.87, 7.57) * mm, "end": v(-18, 7.63) * mm});
            skLineSegment(sketch, "E258", {"start": v(-18, 7.63) * mm, "end": v(-18.56, 7.9) * mm});
            skLineSegment(sketch, "E259", {"start": v(-18.56, 7.9) * mm, "end": v(-18.25, 8.43) * mm});
            skArc(sketch, "E260", {"start": v(-18.25, 8.43) * mm, "mid": v(-18.16, 8.59) * mm, "end": v(-18.09, 8.75) * mm});
            skArc(sketch, "E261", {"start": v(-18.09, 8.75) * mm, "mid": v(-18.04, 8.88) * mm, "end": v(-18, 9.02) * mm});
            skArc(sketch, "E262", {"start": v(-18, 9.02) * mm, "mid": v(-17.97, 9.18) * mm, "end": v(-17.95, 9.34) * mm});
            skArc(sketch, "E263", {"start": v(-17.95, 9.34) * mm, "mid": v(-17.94, 9.57) * mm, "end": v(-17.94, 9.8) * mm});
            skArc(sketch, "E264", {"start": v(-17.94, 9.8) * mm, "mid": v(-17.94, 10.04) * mm, "end": v(-17.95, 10.27) * mm});
            skArc(sketch, "E265", {"start": v(-17.95, 10.27) * mm, "mid": v(-17.97, 10.44) * mm, "end": v(-18, 10.6) * mm});
            skArc(sketch, "E266", {"start": v(-18, 10.6) * mm, "mid": v(-18.05, 10.76) * mm, "end": v(-18.1, 10.9) * mm});
            skArc(sketch, "E267", {"start": v(-18.1, 10.9) * mm, "mid": v(-18.2, 11.1) * mm, "end": v(-18.29, 11.28) * mm});
            skArc(sketch, "E268", {"start": v(-18.29, 11.28) * mm, "mid": v(-18.54, 11.67) * mm, "end": v(-18.83, 12.04) * mm});
            skArc(sketch, "E269", {"start": v(-18.83, 12.04) * mm, "mid": v(-19.14, 12.31) * mm, "end": v(-19.49, 12.53) * mm});
            skArc(sketch, "E270", {"start": v(-19.49, 12.53) * mm, "mid": v(-19.88, 12.7) * mm, "end": v(-20.3, 12.78) * mm});
            skArc(sketch, "E271", {"start": v(-20.3, 12.78) * mm, "mid": v(-20.8, 12.82) * mm, "end": v(-21.32, 12.8) * mm});
            skArc(sketch, "E272", {"start": v(-21.32, 12.8) * mm, "mid": v(-22.07, 12.7) * mm, "end": v(-22.78, 12.45) * mm});
            skArc(sketch, "E273", {"start": v(-22.78, 12.45) * mm, "mid": v(-23.43, 12.09) * mm, "end": v(-24.01, 11.61) * mm});
            skArc(sketch, "E274", {"start": v(-24.01, 11.61) * mm, "mid": v(-24.48, 11.07) * mm, "end": v(-24.83, 10.44) * mm});
            skArc(sketch, "E275", {"start": v(-24.83, 10.44) * mm, "mid": v(-25.05, 9.78) * mm, "end": v(-25.12, 9.1) * mm});
            skArc(sketch, "E276", {"start": v(-25.12, 9.1) * mm, "mid": v(-25.09, 8.63) * mm, "end": v(-25, 8.17) * mm});
            skArc(sketch, "E277", {"start": v(-25, 8.17) * mm, "mid": v(-24.86, 7.7) * mm, "end": v(-24.67, 7.23) * mm});
            skArc(sketch, "E278", {"start": v(-24.67, 7.23) * mm, "mid": v(-24.44, 6.81) * mm, "end": v(-24.18, 6.42) * mm});
            skArc(sketch, "E279", {"start": v(-24.18, 6.42) * mm, "mid": v(-23.9, 6.11) * mm, "end": v(-23.59, 5.86) * mm});
            skArc(sketch, "E280", {"start": v(-23.59, 5.86) * mm, "mid": v(-23.35, 5.72) * mm, "end": v(-23.1, 5.6) * mm});
            skArc(sketch, "E281", {"start": v(-23.1, 5.6) * mm, "mid": v(-22.94, 5.58) * mm, "end": v(-22.77, 5.61) * mm});
            skArc(sketch, "E282", {"start": v(-22.77, 5.61) * mm, "mid": v(-22.64, 5.7) * mm, "end": v(-22.57, 5.85) * mm});
            skArc(sketch, "E283", {"start": v(-22.57, 5.85) * mm, "mid": v(-22.52, 6.1) * mm, "end": v(-22.5, 6.34) * mm});
            skArc(sketch, "E284", {"start": v(-22.5, 6.34) * mm, "mid": v(-22.51, 6.44) * mm, "end": v(-22.53, 6.54) * mm});
            skArc(sketch, "E285", {"start": v(-22.53, 6.54) * mm, "mid": v(-22.55, 6.61) * mm, "end": v(-22.58, 6.68) * mm});
            skArc(sketch, "E286", {"start": v(-22.58, 6.68) * mm, "mid": v(-22.63, 6.74) * mm, "end": v(-22.7, 6.79) * mm});
            skArc(sketch, "E287", {"start": v(-22.7, 6.79) * mm, "mid": v(-22.79, 6.85) * mm, "end": v(-22.89, 6.9) * mm});
            skArc(sketch, "E288", {"start": v(-22.89, 6.9) * mm, "mid": v(-23.08, 7.02) * mm, "end": v(-23.25, 7.18) * mm});
            skArc(sketch, "E289", {"start": v(-23.25, 7.18) * mm, "mid": v(-23.41, 7.41) * mm, "end": v(-23.56, 7.66) * mm});
            skArc(sketch, "E290", {"start": v(-23.56, 7.66) * mm, "mid": v(-23.68, 7.97) * mm, "end": v(-23.78, 8.29) * mm});
            skArc(sketch, "E291", {"start": v(-23.78, 8.29) * mm, "mid": v(-23.85, 8.62) * mm, "end": v(-23.9, 8.97) * mm});
            skArc(sketch, "E292", {"start": v(-23.9, 8.97) * mm, "mid": v(-23.9, 9.16) * mm, "end": v(-23.9, 9.36) * mm});
            skArc(sketch, "E293", {"start": v(-23.9, 9.36) * mm, "mid": v(-23.9, 9.5) * mm, "end": v(-23.88, 9.65) * mm});
            skArc(sketch, "E294", {"start": v(-23.88, 9.65) * mm, "mid": v(-23.85, 9.79) * mm, "end": v(-23.8, 9.92) * mm});
            skArc(sketch, "E295", {"start": v(-23.8, 9.92) * mm, "mid": v(-23.74, 10.07) * mm, "end": v(-23.67, 10.22) * mm});
            skArc(sketch, "E296", {"start": v(-23.67, 10.22) * mm, "mid": v(-23.44, 10.59) * mm, "end": v(-23.13, 10.9) * mm});
            skArc(sketch, "E297", {"start": v(-23.13, 10.9) * mm, "mid": v(-22.73, 11.18) * mm, "end": v(-22.3, 11.42) * mm});
            skArc(sketch, "E298", {"start": v(-22.3, 11.42) * mm, "mid": v(-21.83, 11.6) * mm, "end": v(-21.36, 11.7) * mm});
            skArc(sketch, "E299", {"start": v(-21.36, 11.7) * mm, "mid": v(-20.93, 11.72) * mm, "end": v(-20.52, 11.66) * mm});
            skArc(sketch, "E300", {"start": v(-20.52, 11.66) * mm, "mid": v(-20.17, 11.52) * mm, "end": v(-19.86, 11.31) * mm});
            skArc(sketch, "E301", {"start": v(-19.86, 11.31) * mm, "mid": v(-19.58, 11.04) * mm, "end": v(-19.36, 10.71) * mm});
            skArc(sketch, "E302", {"start": v(-19.36, 10.71) * mm, "mid": v(-19.2, 10.35) * mm, "end": v(-19.12, 9.96) * mm});
            skArc(sketch, "E303", {"start": v(-19.12, 9.96) * mm, "mid": v(-19.1, 9.57) * mm, "end": v(-19.17, 9.18) * mm});
            skArc(sketch, "E304", {"start": v(-19.17, 9.18) * mm, "mid": v(-19.24, 8.98) * mm, "end": v(-19.34, 8.78) * mm});
            skArc(sketch, "E305", {"start": v(-19.34, 8.78) * mm, "mid": v(-19.48, 8.58) * mm, "end": v(-19.64, 8.38) * mm});
            skArc(sketch, "E306", {"start": v(-19.64, 8.38) * mm, "mid": v(-19.82, 8.2) * mm, "end": v(-20, 8.05) * mm});
            skArc(sketch, "E307", {"start": v(-20, 8.05) * mm, "mid": v(-20.16, 7.95) * mm, "end": v(-20.33, 7.89) * mm});
            skArc(sketch, "E308", {"start": v(-20.33, 7.89) * mm, "mid": v(-20.4, 7.87) * mm, "end": v(-20.46, 7.84) * mm});
            skArc(sketch, "E309", {"start": v(-20.46, 7.84) * mm, "mid": v(-20.5, 7.8) * mm, "end": v(-20.54, 7.76) * mm});
            skArc(sketch, "E310", {"start": v(-20.54, 7.76) * mm, "mid": v(-20.57, 7.71) * mm, "end": v(-20.59, 7.65) * mm});
            skArc(sketch, "E311", {"start": v(-20.59, 7.65) * mm, "mid": v(-20.6, 7.57) * mm, "end": v(-20.6, 7.5) * mm});
            skArc(sketch, "E312", {"start": v(-20.6, 7.5) * mm, "mid": v(-20.59, 7.33) * mm, "end": v(-20.54, 7.17) * mm});
            skArc(sketch, "E313", {"start": v(-20.54, 7.17) * mm, "mid": v(-20.46, 7.04) * mm, "end": v(-20.35, 6.95) * mm});
            skArc(sketch, "E314", {"start": v(-20.35, 6.95) * mm, "mid": v(-20.2, 6.88) * mm, "end": v(-20.05, 6.84) * mm});
            skArc(sketch, "E315", {"start": v(-20.05, 6.84) * mm, "mid": v(-19.83, 6.83) * mm, "end": v(-19.62, 6.85) * mm});
            skArc(sketch, "E316", {"start": v(-19.62, 6.85) * mm, "mid": v(-19.36, 6.87) * mm, "end": v(-19.1, 6.87) * mm});
            skArc(sketch, "E317", {"start": v(-19.1, 6.87) * mm, "mid": v(-18.89, 6.83) * mm, "end": v(-18.68, 6.76) * mm});
            skArc(sketch, "E318", {"start": v(-18.68, 6.76) * mm, "mid": v(-18.5, 6.66) * mm, "end": v(-18.35, 6.53) * mm});
            skArc(sketch, "E319", {"start": v(-18.35, 6.53) * mm, "mid": v(-18.21, 6.35) * mm, "end": v(-18.1, 6.16) * mm});
            skArc(sketch, "E320", {"start": v(-18.1, 6.16) * mm, "mid": v(-18, 5.95) * mm, "end": v(-17.94, 5.74) * mm});
            skArc(sketch, "E321", {"start": v(-17.94, 5.74) * mm, "mid": v(-17.92, 5.55) * mm, "end": v(-17.93, 5.36) * mm});
            skArc(sketch, "E322", {"start": v(-17.93, 5.36) * mm, "mid": v(-17.99, 5.18) * mm, "end": v(-18.08, 5.02) * mm});
            skArc(sketch, "E323", {"start": v(-18.08, 5.02) * mm, "mid": v(-18.2, 4.85) * mm, "end": v(-18.36, 4.7) * mm});
            skArc(sketch, "E324", {"start": v(-18.36, 4.7) * mm, "mid": v(-18.55, 4.57) * mm, "end": v(-18.75, 4.47) * mm});
            skArc(sketch, "E325", {"start": v(-18.75, 4.47) * mm, "mid": v(-18.93, 4.41) * mm, "end": v(-19.13, 4.4) * mm});
            skArc(sketch, "E326", {"start": v(-19.13, 4.4) * mm, "mid": v(-19.32, 4.43) * mm, "end": v(-19.5, 4.5) * mm});
            skArc(sketch, "E327", {"start": v(-19.5, 4.5) * mm, "mid": v(-19.67, 4.61) * mm, "end": v(-19.81, 4.76) * mm});
            skArc(sketch, "E328", {"start": v(-19.81, 4.76) * mm, "mid": v(-19.94, 4.93) * mm, "end": v(-20.05, 5.11) * mm});
            skArc(sketch, "E329", {"start": v(-20.05, 5.11) * mm, "mid": v(-20.18, 5.39) * mm, "end": v(-20.3, 5.66) * mm});
            skArc(sketch, "E330", {"start": v(-20.3, 5.66) * mm, "mid": v(-20.48, 6.13) * mm, "end": v(-20.66, 6.6) * mm});
            skArc(sketch, "E331", {"start": v(-20.66, 6.6) * mm, "mid": v(-21, 7.57) * mm, "end": v(-21.36, 8.56) * mm});
            skArc(sketch, "E332", {"start": v(-21.36, 8.56) * mm, "mid": v(-21.58, 9.17) * mm, "end": v(-21.82, 9.78) * mm});
            skArc(sketch, "E333", {"start": v(-21.82, 9.78) * mm, "mid": v(-21.95, 10.05) * mm, "end": v(-22.12, 10.3) * mm});
            skArc(sketch, "E334", {"start": v(-22.12, 10.3) * mm, "mid": v(-22.27, 10.42) * mm, "end": v(-22.44, 10.48) * mm});
            skArc(sketch, "E335", {"start": v(-22.44, 10.48) * mm, "mid": v(-22.67, 10.48) * mm, "end": v(-22.89, 10.43) * mm});
            skArc(sketch, "E336", {"start": v(-22.89, 10.43) * mm, "mid": v(-23, 10.38) * mm, "end": v(-23.1, 10.3) * mm});
            skArc(sketch, "E337", {"start": v(-23.1, 10.3) * mm, "mid": v(-23.16, 10.23) * mm, "end": v(-23.18, 10.13) * mm});
            skArc(sketch, "E338", {"start": v(-23.18, 10.13) * mm, "mid": v(-23.16, 9.98) * mm, "end": v(-23.12, 9.82) * mm});
            skArc(sketch, "E339", {"start": v(-23.12, 9.82) * mm, "mid": v(-22.96, 9.4) * mm, "end": v(-22.8, 8.98) * mm});
            skArc(sketch, "E340", {"start": v(-22.8, 8.98) * mm, "mid": v(-22.73, 8.77) * mm, "end": v(-22.66, 8.57) * mm});
            skArc(sketch, "E341", {"start": v(-22.66, 8.57) * mm, "mid": v(-22.56, 8.3) * mm, "end": v(-22.46, 8.02) * mm});
            skArc(sketch, "E342", {"start": v(-22.46, 8.02) * mm, "mid": v(-22.35, 7.73) * mm, "end": v(-22.25, 7.43) * mm});
            skArc(sketch, "E343", {"start": v(-22.25, 7.43) * mm, "mid": v(-22.16, 7.17) * mm, "end": v(-22.06, 6.9) * mm});
            skArc(sketch, "E344", {"start": v(-22.06, 6.9) * mm, "mid": v(-21.88, 6.36) * mm, "end": v(-21.68, 5.83) * mm});
            skArc(sketch, "E345", {"start": v(-21.68, 5.83) * mm, "mid": v(-21.52, 5.42) * mm, "end": v(-21.36, 5.02) * mm});
            skArc(sketch, "E346", {"start": v(-21.36, 5.02) * mm, "mid": v(-21.22, 4.71) * mm, "end": v(-21.06, 4.42) * mm});
            skArc(sketch, "E347", {"start": v(-21.06, 4.42) * mm, "mid": v(-20.94, 4.2) * mm, "end": v(-20.8, 4) * mm});
            skArc(sketch, "E348", {"start": v(-18.93, 2.93) * mm, "mid": v(-19, 3.1) * mm, "end": v(-19.05, 3.28) * mm});
            skArc(sketch, "E349", {"start": v(-19.05, 3.28) * mm, "mid": v(-19.06, 3.3) * mm, "end": v(-19.06, 3.3) * mm});
            skArc(sketch, "E350", {"start": v(-19.06, 3.3) * mm, "mid": v(-19.06, 3.3) * mm, "end": v(-19.05, 3.31) * mm});
            skArc(sketch, "E351", {"start": v(-19.05, 3.31) * mm, "mid": v(-19.02, 3.32) * mm, "end": v(-19, 3.32) * mm});
            skArc(sketch, "E352", {"start": v(-19, 3.32) * mm, "mid": v(-18.96, 3.33) * mm, "end": v(-18.93, 3.33) * mm});
            skArc(sketch, "E353", {"start": v(-18.93, 3.33) * mm, "mid": v(-18.9, 3.33) * mm, "end": v(-18.85, 3.33) * mm});
            skArc(sketch, "E354", {"start": v(-18.85, 3.33) * mm, "mid": v(-18.68, 3.35) * mm, "end": v(-18.52, 3.4) * mm});
            skArc(sketch, "E355", {"start": v(-18.52, 3.4) * mm, "mid": v(-18.28, 3.5) * mm, "end": v(-18.05, 3.61) * mm});
            skArc(sketch, "E356", {"start": v(-18.05, 3.61) * mm, "mid": v(-17.82, 3.74) * mm, "end": v(-17.6, 3.89) * mm});
            skArc(sketch, "E357", {"start": v(-17.6, 3.89) * mm, "mid": v(-17.43, 4.02) * mm, "end": v(-17.27, 4.17) * mm});
            skLineSegment(sketch, "E358", {"start": v(-17.27, 4.17) * mm, "end": v(-16.93, 4.53) * mm});
            skLineSegment(sketch, "E359", {"start": v(-16.93, 4.53) * mm, "end": v(-16.38, 4.1) * mm});
            skArc(sketch, "E360", {"start": v(-16.38, 4.1) * mm, "mid": v(-16.26, 4.02) * mm, "end": v(-16.13, 3.94) * mm});
            skArc(sketch, "E361", {"start": v(-16.13, 3.94) * mm, "mid": v(-15.99, 3.85) * mm, "end": v(-15.84, 3.77) * mm});
            skArc(sketch, "E362", {"start": v(-15.84, 3.77) * mm, "mid": v(-15.7, 3.7) * mm, "end": v(-15.55, 3.63) * mm});
            skArc(sketch, "E363", {"start": v(-15.55, 3.63) * mm, "mid": v(-15.43, 3.59) * mm, "end": v(-15.3, 3.55) * mm});
            skArc(sketch, "E364", {"start": v(-15.3, 3.55) * mm, "mid": v(-15.2, 3.53) * mm, "end": v(-15.1, 3.5) * mm});
            skArc(sketch, "E365", {"start": v(-15.1, 3.5) * mm, "mid": v(-15.02, 3.47) * mm, "end": v(-14.93, 3.45) * mm});
            skArc(sketch, "E366", {"start": v(-14.93, 3.45) * mm, "mid": v(-14.87, 3.42) * mm, "end": v(-14.8, 3.4) * mm});
            skArc(sketch, "E367", {"start": v(-14.8, 3.4) * mm, "mid": v(-14.79, 3.39) * mm, "end": v(-14.78, 3.37) * mm});
            skArc(sketch, "E368", {"start": v(-14.78, 3.37) * mm, "mid": v(-14.78, 3.35) * mm, "end": v(-14.79, 3.34) * mm});
            skArc(sketch, "E369", {"start": v(-14.79, 3.34) * mm, "mid": v(-14.8, 3.29) * mm, "end": v(-14.83, 3.24) * mm});
            skArc(sketch, "E370", {"start": v(-14.83, 3.24) * mm, "mid": v(-14.85, 3.18) * mm, "end": v(-14.88, 3.13) * mm});
            skArc(sketch, "E371", {"start": v(-14.88, 3.13) * mm, "mid": v(-14.91, 3.06) * mm, "end": v(-14.94, 3) * mm});
            skArc(sketch, "E372", {"start": v(-13.31, 3.7) * mm, "mid": v(-13, 4.17) * mm, "end": v(-12.7, 4.63) * mm});
            skArc(sketch, "E373", {"start": v(-12.7, 4.63) * mm, "mid": v(-12.58, 4.83) * mm, "end": v(-12.48, 5.03) * mm});
            skArc(sketch, "E374", {"start": v(-12.48, 5.03) * mm, "mid": v(-12.42, 5.19) * mm, "end": v(-12.38, 5.35) * mm});
            skArc(sketch, "E375", {"start": v(-12.38, 5.35) * mm, "mid": v(-12.36, 5.57) * mm, "end": v(-12.35, 5.78) * mm});
            skArc(sketch, "E376", {"start": v(-12.35, 5.78) * mm, "mid": v(-12.36, 5.93) * mm, "end": v(-12.37, 6.08) * mm});
            skArc(sketch, "E377", {"start": v(-12.37, 6.08) * mm, "mid": v(-12.38, 6.2) * mm, "end": v(-12.4, 6.32) * mm});
            skArc(sketch, "E378", {"start": v(-12.4, 6.32) * mm, "mid": v(-12.43, 6.41) * mm, "end": v(-12.47, 6.5) * mm});
            skArc(sketch, "E379", {"start": v(-12.47, 6.5) * mm, "mid": v(-12.52, 6.58) * mm, "end": v(-12.58, 6.65) * mm});
            skArc(sketch, "E380", {"start": v(-12.58, 6.65) * mm, "mid": v(-12.65, 6.73) * mm, "end": v(-12.71, 6.81) * mm});
            skArc(sketch, "E381", {"start": v(-12.71, 6.81) * mm, "mid": v(-12.72, 6.84) * mm, "end": v(-12.71, 6.87) * mm});
            skArc(sketch, "E382", {"start": v(-12.71, 6.87) * mm, "mid": v(-12.68, 6.89) * mm, "end": v(-12.65, 6.9) * mm});
            skArc(sketch, "E383", {"start": v(-12.65, 6.9) * mm, "mid": v(-12.49, 6.9) * mm, "end": v(-12.33, 6.9) * mm});
            skArc(sketch, "E384", {"start": v(-12.33, 6.9) * mm, "mid": v(-12.22, 6.9) * mm, "end": v(-12.11, 6.92) * mm});
            skArc(sketch, "E385", {"start": v(-12.11, 6.92) * mm, "mid": v(-11.97, 6.95) * mm, "end": v(-11.83, 6.98) * mm});
            skArc(sketch, "E386", {"start": v(-11.83, 6.98) * mm, "mid": v(-11.68, 7.02) * mm, "end": v(-11.54, 7.07) * mm});
            skArc(sketch, "E387", {"start": v(-11.54, 7.07) * mm, "mid": v(-11.4, 7.12) * mm, "end": v(-11.28, 7.18) * mm});
            skArc(sketch, "E388", {"start": v(-11.28, 7.18) * mm, "mid": v(-10.71, 7.51) * mm, "end": v(-10.22, 7.96) * mm});
            skArc(sketch, "E389", {"start": v(-10.22, 7.96) * mm, "mid": v(-9.84, 8.48) * mm, "end": v(-9.58, 9.08) * mm});
            skArc(sketch, "E390", {"start": v(-9.58, 9.08) * mm, "mid": v(-9.46, 9.7) * mm, "end": v(-9.47, 10.32) * mm});
            skArc(sketch, "E391", {"start": v(-9.47, 10.32) * mm, "mid": v(-9.61, 10.91) * mm, "end": v(-9.9, 11.45) * mm});
            skArc(sketch, "E392", {"start": v(-9.9, 11.45) * mm, "mid": v(-10.09, 11.7) * mm, "end": v(-10.3, 11.93) * mm});
            skArc(sketch, "E393", {"start": v(-10.3, 11.93) * mm, "mid": v(-10.59, 12.17) * mm, "end": v(-10.88, 12.39) * mm});
            skArc(sketch, "E394", {"start": v(-10.88, 12.39) * mm, "mid": v(-11.2, 12.6) * mm, "end": v(-11.53, 12.78) * mm});
            skArc(sketch, "E395", {"start": v(-11.53, 12.78) * mm, "mid": v(-11.83, 12.92) * mm, "end": v(-12.15, 13.03) * mm});
            skArc(sketch, "E396", {"start": v(-12.15, 13.03) * mm, "mid": v(-12.45, 13.1) * mm, "end": v(-12.76, 13.15) * mm});
            skArc(sketch, "E397", {"start": v(-12.76, 13.15) * mm, "mid": v(-13.12, 13.18) * mm, "end": v(-13.5, 13.18) * mm});
            skArc(sketch, "E398", {"start": v(-13.5, 13.18) * mm, "mid": v(-13.85, 13.16) * mm, "end": v(-14.2, 13.12) * mm});
            skArc(sketch, "E399", {"start": v(-14.2, 13.12) * mm, "mid": v(-14.48, 13.07) * mm, "end": v(-14.75, 12.98) * mm});
            skArc(sketch, "E400", {"start": v(-14.78, 3.37) * mm, "mid": v(-14.03, 3.46) * mm, "end": v(-13.31, 3.7) * mm});
            skArc(sketch, "E401", {"start": v(-20.8, 4) * mm, "mid": v(-20, 3.48) * mm, "end": v(-19.06, 3.3) * mm});
            skSolve(sketch);
        }
        {
            var Q0;
            Q0 = qSketchRegion(id + "F4", true);
            extrude(context, id + "F5", {"entities" : qUnion([Q0]), "depth" : 1 * mm, "offsetDistance" : 25.4 * mm});
        }
        {
            var Q0;
            Q0=qCreatedBy(makeId("Top.planeOp"),FACE);
            var sketch = newSketch(context, id + "F6", { "sketchPlane" : qUnion([Q0])});
            skCircle(sketch, "E402", {"center": v(-17.27, 19.39) * mm, "radius": 0.5 * mm});
            skSolve(sketch);
        }
        {
            var Q0;
            Q0 = qSketchRegion(id + "F6", true);
            extrude(context, id + "F7", {"entities" : qUnion([Q0]), "operationType" : NewBodyOperationType.REMOVE, "depth" : 25.4 * mm, "offsetDistance" : 25.4 * mm});
        }
        {
            var Q0;
            Q0 = qSketchRegion(id + "F6", true);
            extrude(context, id + "F8", {"entities" : qUnion([Q0]), "operationType" : NewBodyOperationType.REMOVE, "oppositeDirection" : true, "depth" : 25.4 * mm, "offsetDistance" : 25.4 * mm});
        }
    });
